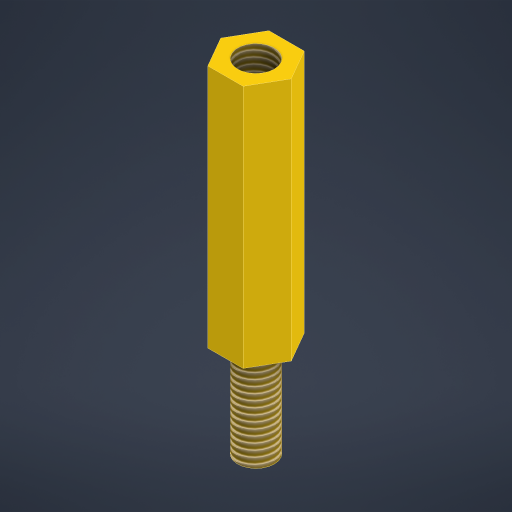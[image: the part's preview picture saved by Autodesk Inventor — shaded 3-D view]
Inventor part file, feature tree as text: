
AUTODESK INVENTOR PART (.ipt)
format: ipt  version: 2024 (Build 280153000, 153)  size: 221,184 bytes
history: native  units: mm
features: other x3, extrude x3, sketch x3
ambient origin geometry x8: Origin, YZ Plane, XZ Plane, XY Plane, X Axis, Y Axis, Z Axis, Center Point
bodies: Body1 (feature_tree)
feature tree (9):
  other  "Těleso1"
  extrude  "Vysunutí1"  Depth=5.0mm
  extrude  "Vysunutí2"  Depth=20.0mm TaperAngle=0.0deg
  other  "Závit1"
  extrude  "Vysunutí3"  Depth=3.0mm
  other  "Závit2"
  sketch  "Náčrt1"
  sketch  "Náčrt2"
  sketch  "Náčrt3"
